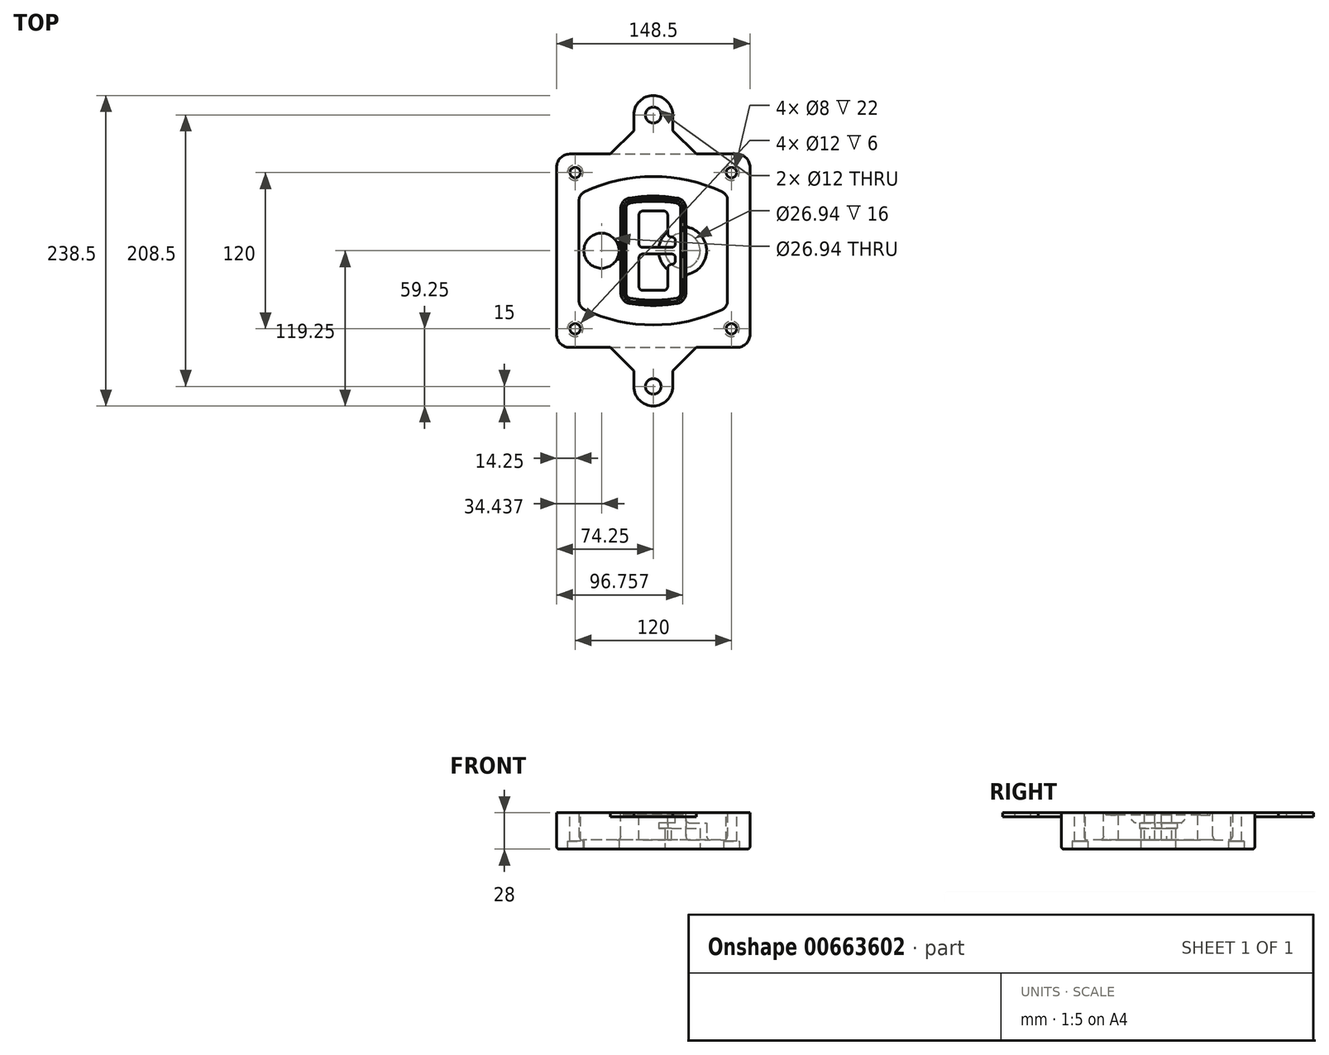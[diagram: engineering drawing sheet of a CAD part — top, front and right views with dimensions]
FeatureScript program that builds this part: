
annotation { "Feature Type Name" : "Feature", "Feature Type Description" : "" }
export const myFeature = defineFeature(function(context is Context, id is Id, definition is map)
    precondition{}
    {
        {
            var Q0;
            Q0=qCreatedBy(makeId("Top.planeOp"),FACE);
            var sketch = newSketch(context, id + "F0", { "sketchPlane" : qUnion([Q0])});
            skPoint(sketch, "E0.rect.middle", {"position": v(0, 0) * mm});
            skLineSegment(sketch, "E1.bottom", {"start": v(-64.25, -74.25) * mm, "end": v(64.25, -74.25) * mm});
            skLineSegment(sketch, "E1.top", {"start": v(-64.25, 74.25) * mm, "end": v(64.25, 74.25) * mm});
            skLineSegment(sketch, "E1.left", {"start": v(-74.25, -64.25) * mm, "end": v(-74.25, 64.25) * mm});
            skLineSegment(sketch, "E1.right", {"start": v(74.25, -64.25) * mm, "end": v(74.25, 64.25) * mm});
            skLineSegment(sketch, "E2", {"start": v(-74.25, 74.25) * mm, "end": v(74.25, -74.25) * mm, "construction": true});
            skLineSegment(sketch, "E3", {"start": v(74.25, 74.25) * mm, "end": v(-74.25, -74.25) * mm, "construction": true});
            skCircle(sketch, "E4", {"center": v(-60, 60) * mm, "radius": 4 * mm});
            skCircle(sketch, "E5", {"center": v(60, 60) * mm, "radius": 4 * mm});
            skCircle(sketch, "E6", {"center": v(60, -60) * mm, "radius": 4 * mm});
            skCircle(sketch, "E7", {"center": v(-60, -60) * mm, "radius": 4 * mm});
            skLineSegment(sketch, "E8", {"start": v(-60, 60) * mm, "end": v(60, 60) * mm, "construction": true});
            skLineSegment(sketch, "E9", {"start": v(60, 60) * mm, "end": v(60, -60) * mm, "construction": true});
            skLineSegment(sketch, "E10", {"start": v(60, -60) * mm, "end": v(-60, -60) * mm, "construction": true});
            skLineSegment(sketch, "E11", {"start": v(-60, -60) * mm, "end": v(-60, 60) * mm, "construction": true});
            skLineSegment(sketch, "E12", {"start": v(-60, 38.83) * mm, "end": v(-60, -38.83) * mm});
            skLineSegment(sketch, "E13", {"start": v(60, 38.83) * mm, "end": v(60, -38.83) * mm});
            skArc(sketch, "E14", {"start": v(54.26, 47.88) * mm, "mid": v(0, 60) * mm, "end": v(-54.26, 47.88) * mm});
            skArc(sketch, "E15", {"start": v(-54.26, -47.88) * mm, "mid": v(0, -60) * mm, "end": v(54.26, -47.88) * mm});
            skLineSegment(sketch, "E16", {"start": v(-60, 0) * mm, "end": v(60, 0) * mm, "construction": true});
            skPoint(sketch, "E17.visualSharp", {"position": v(-60, -45) * mm});
            skArc(sketch, "E17.filletArc", {"start": v(-60, -38.83) * mm, "mid": v(-58.44, -44.2) * mm, "end": v(-54.26, -47.88) * mm});
            skPoint(sketch, "E18.visualSharp", {"position": v(-60, 45) * mm});
            skArc(sketch, "E18.filletArc", {"start": v(-54.26, 47.88) * mm, "mid": v(-58.44, 44.2) * mm, "end": v(-60, 38.83) * mm});
            skPoint(sketch, "E19.visualSharp", {"position": v(60, 45) * mm});
            skArc(sketch, "E19.filletArc", {"start": v(60, 38.83) * mm, "mid": v(58.44, 44.2) * mm, "end": v(54.26, 47.88) * mm});
            skPoint(sketch, "E20.visualSharp", {"position": v(60, -45) * mm});
            skArc(sketch, "E20.filletArc", {"start": v(54.26, -47.88) * mm, "mid": v(58.44, -44.2) * mm, "end": v(60, -38.83) * mm});
            skPoint(sketch, "E21.visualSharp", {"position": v(-74.25, 74.25) * mm});
            skArc(sketch, "E21.filletArc", {"start": v(-64.25, 74.25) * mm, "mid": v(-71.32, 71.32) * mm, "end": v(-74.25, 64.25) * mm});
            skPoint(sketch, "E22.visualSharp", {"position": v(74.25, 74.25) * mm});
            skArc(sketch, "E22.filletArc", {"start": v(74.25, 64.25) * mm, "mid": v(71.32, 71.32) * mm, "end": v(64.25, 74.25) * mm});
            skPoint(sketch, "E23.visualSharp", {"position": v(74.25, -74.25) * mm});
            skArc(sketch, "E23.filletArc", {"start": v(64.25, -74.25) * mm, "mid": v(71.32, -71.32) * mm, "end": v(74.25, -64.25) * mm});
            skPoint(sketch, "E24.visualSharp", {"position": v(-74.25, -74.25) * mm});
            skArc(sketch, "E24.filletArc", {"start": v(-74.25, -64.25) * mm, "mid": v(-71.32, -71.32) * mm, "end": v(-64.25, -74.25) * mm});
            skArc(sketch, "E25.0", {"start": v(57, 38.83) * mm, "mid": v(55.9, 42.58) * mm, "end": v(52.98, 45.17) * mm});
            skLineSegment(sketch, "E25.1", {"start": v(57, 38.83) * mm, "end": v(57, -38.83) * mm});
            skArc(sketch, "E25.2", {"start": v(52.98, -45.17) * mm, "mid": v(55.9, -42.58) * mm, "end": v(57, -38.83) * mm});
            skArc(sketch, "E25.3", {"start": v(-52.98, -45.17) * mm, "mid": v(0, -57) * mm, "end": v(52.98, -45.17) * mm});
            skArc(sketch, "E25.4", {"start": v(-57, -38.83) * mm, "mid": v(-55.9, -42.58) * mm, "end": v(-52.98, -45.17) * mm});
            skArc(sketch, "E25.5", {"start": v(52.98, 45.17) * mm, "mid": v(0, 57) * mm, "end": v(-52.98, 45.17) * mm});
            skLineSegment(sketch, "E25.6", {"start": v(-57, 38.83) * mm, "end": v(-57, -38.83) * mm});
            skArc(sketch, "E25.7", {"start": v(-52.98, 45.17) * mm, "mid": v(-55.9, 42.58) * mm, "end": v(-57, 38.83) * mm});
            skArc(sketch, "E26.0", {"start": v(-55.96, 51.5) * mm, "mid": v(-61.82, 46.33) * mm, "end": v(-64, 38.83) * mm});
            skArc(sketch, "E26.1", {"start": v(55.96, 51.5) * mm, "mid": v(0, 64) * mm, "end": v(-55.96, 51.5) * mm});
            skArc(sketch, "E26.2", {"start": v(64, 38.83) * mm, "mid": v(61.82, 46.33) * mm, "end": v(55.96, 51.5) * mm});
            skLineSegment(sketch, "E26.3", {"start": v(64, 38.83) * mm, "end": v(64, -38.83) * mm});
            skArc(sketch, "E26.4", {"start": v(55.96, -51.5) * mm, "mid": v(61.82, -46.33) * mm, "end": v(64, -38.83) * mm});
            skLineSegment(sketch, "E26.5", {"start": v(-64, 38.83) * mm, "end": v(-64, -38.83) * mm});
            skArc(sketch, "E26.6", {"start": v(-55.96, -51.5) * mm, "mid": v(0, -64) * mm, "end": v(55.96, -51.5) * mm});
            skArc(sketch, "E26.7", {"start": v(-64, -38.83) * mm, "mid": v(-61.82, -46.33) * mm, "end": v(-55.96, -51.5) * mm});
            skSolve(sketch);
        }
        {
            var Q0;
            Q0=makeQuery(id+"F0.imprint","IMPRINT",FACE,{"disambiguationData":[TD([[makeQuery(id+"F0.imprint","IMPRINT",EDGE,{"derivedFrom":sQuery(id+"F0.wireOp",EDGE,"E1.bottom")}),1.0]])]});
            var Q1;
            Q1=makeQuery(id+"F0.imprint","IMPRINT",FACE,{"disambiguationData":[TD([[makeQuery(id+"F0.imprint","IMPRINT",EDGE,{"derivedFrom":sQuery(id+"F0.wireOp",EDGE,"E12")}),1.0]])]});
            var Q2;
            Q2=makeQuery(id+"F0.imprint","IMPRINT",FACE,{"disambiguationData":[TD([[makeQuery(id+"F0.imprint","IMPRINT",EDGE,{"derivedFrom":sQuery(id+"F0.wireOp",EDGE,"E25.0")}),1.0]])]});
            var Q3;
            Q3=makeQuery(id+"F0.imprint","IMPRINT",FACE,{"disambiguationData":[TD([[makeQuery(id+"F0.imprint","IMPRINT",EDGE,{"derivedFrom":sQuery(id+"F0.wireOp",EDGE,"E12")}),-1.0]])]});
            extrude(context, id + "F1", {"entities" : qUnion([Q0, Q1, Q2, Q3]), "oppositeDirection" : true, "depth" : 25 * mm});
        }
        {
            var Q0;
            Q0=makeQuery(id+"F0.imprint","IMPRINT",FACE,{"disambiguationData":[TD([[makeQuery(id+"F0.imprint","IMPRINT",EDGE,{"derivedFrom":sQuery(id+"F0.wireOp",EDGE,"E12")}),1.0]])]});
            extrude(context, id + "F2", {"entities" : qUnion([Q0]), "operationType" : NewBodyOperationType.ADD, "depth" : 3 * mm});
        }
        {
            var Q0;
            Q0=makeQuery(id+"F0.imprint","IMPRINT",FACE,{"disambiguationData":[TD([[makeQuery(id+"F0.imprint","IMPRINT",EDGE,{"derivedFrom":sQuery(id+"F0.wireOp",EDGE,"E25.0")}),1.0]])]});
            extrude(context, id + "F3", {"entities" : qUnion([Q0]), "operationType" : NewBodyOperationType.REMOVE, "oppositeDirection" : true, "depth" : 18 * mm});
        }
        {
            var Q0;
            Q0=makeQuery(id+"F2.opExtrude","CAP_FACE",FACE,{"disambiguationData":[OSD([sQuery(id+"F0.wireOp",EDGE,"E12"),sQuery(id+"F0.wireOp",EDGE,"E13"),sQuery(id+"F0.wireOp",EDGE,"E14"),sQuery(id+"F0.wireOp",EDGE,"E15"),sQuery(id+"F0.wireOp",EDGE,"E17.filletArc"),sQuery(id+"F0.wireOp",EDGE,"E18.filletArc"),sQuery(id+"F0.wireOp",EDGE,"E19.filletArc"),sQuery(id+"F0.wireOp",EDGE,"E20.filletArc"),sQuery(id+"F0.wireOp",EDGE,"E25.0"),sQuery(id+"F0.wireOp",EDGE,"E25.1"),sQuery(id+"F0.wireOp",EDGE,"E25.2"),sQuery(id+"F0.wireOp",EDGE,"E25.3"),sQuery(id+"F0.wireOp",EDGE,"E25.4"),sQuery(id+"F0.wireOp",EDGE,"E25.5"),sQuery(id+"F0.wireOp",EDGE,"E25.6"),sQuery(id+"F0.wireOp",EDGE,"E25.7")])],"isStart":false});
            var sketch = newSketch(context, id + "F4", { "sketchPlane" : qUnion([Q0])});
            skArc(sketch, "E27.0", {"start": v(-18.34, -40.45) * mm, "mid": v(0, -42) * mm, "end": v(18.34, -40.45) * mm});
            skArc(sketch, "E28.0", {"start": v(18.34, 40.45) * mm, "mid": v(0, 42) * mm, "end": v(-18.34, 40.45) * mm});
            skLineSegment(sketch, "E29", {"start": v(-25, 32.57) * mm, "end": v(-25, -32.57) * mm});
            skLineSegment(sketch, "E30", {"start": v(25, 32.57) * mm, "end": v(25, -32.57) * mm});
            skLineSegment(sketch, "E31", {"start": v(-25, 39.1) * mm, "end": v(25, 39.1) * mm, "construction": true});
            skLineSegment(sketch, "E32", {"start": v(-25, -39.1) * mm, "end": v(25, -39.1) * mm, "construction": true});
            skPoint(sketch, "E33.visualSharp", {"position": v(-25, 39.1) * mm});
            skArc(sketch, "E33.filletArc", {"start": v(-18.34, 40.45) * mm, "mid": v(-23.11, 37.73) * mm, "end": v(-25, 32.57) * mm});
            skPoint(sketch, "E34.visualSharp", {"position": v(25, 39.1) * mm});
            skArc(sketch, "E34.filletArc", {"start": v(25, 32.57) * mm, "mid": v(23.11, 37.73) * mm, "end": v(18.34, 40.45) * mm});
            skPoint(sketch, "E35.visualSharp", {"position": v(25, -39.1) * mm});
            skArc(sketch, "E35.filletArc", {"start": v(18.34, -40.45) * mm, "mid": v(23.11, -37.73) * mm, "end": v(25, -32.57) * mm});
            skPoint(sketch, "E36.visualSharp", {"position": v(-25, -39.1) * mm});
            skArc(sketch, "E36.filletArc", {"start": v(-25, -32.57) * mm, "mid": v(-23.11, -37.73) * mm, "end": v(-18.34, -40.45) * mm});
            skArc(sketch, "E37.0", {"start": v(52.98, 45.17) * mm, "mid": v(0, 57) * mm, "end": v(-52.98, 45.17) * mm});
            skArc(sketch, "E37.1", {"start": v(-52.98, 45.17) * mm, "mid": v(-55.9, 42.58) * mm, "end": v(-57, 38.83) * mm});
            skLineSegment(sketch, "E37.2", {"start": v(-57, 38.83) * mm, "end": v(-57, -38.83) * mm});
            skArc(sketch, "E37.3", {"start": v(-57, -38.83) * mm, "mid": v(-55.9, -42.58) * mm, "end": v(-52.98, -45.17) * mm});
            skArc(sketch, "E37.4", {"start": v(-52.98, -45.17) * mm, "mid": v(0, -57) * mm, "end": v(52.98, -45.17) * mm});
            skArc(sketch, "E37.5", {"start": v(52.98, -45.17) * mm, "mid": v(55.9, -42.58) * mm, "end": v(57, -38.83) * mm});
            skLineSegment(sketch, "E37.6", {"start": v(57, 38.83) * mm, "end": v(57, -38.83) * mm});
            skArc(sketch, "E37.7", {"start": v(57, 38.83) * mm, "mid": v(55.9, 42.58) * mm, "end": v(52.98, 45.17) * mm});
            skLineSegment(sketch, "E38.0", {"start": v(23, 32.57) * mm, "end": v(23, -32.57) * mm});
            skArc(sketch, "E38.1", {"start": v(18, -38.48) * mm, "mid": v(21.58, -36.44) * mm, "end": v(23, -32.57) * mm});
            skArc(sketch, "E38.2", {"start": v(-18, -38.48) * mm, "mid": v(0, -40) * mm, "end": v(18, -38.48) * mm});
            skArc(sketch, "E38.3", {"start": v(-23, -32.57) * mm, "mid": v(-21.58, -36.44) * mm, "end": v(-18, -38.48) * mm});
            skLineSegment(sketch, "E38.4", {"start": v(-23, 32.57) * mm, "end": v(-23, -32.57) * mm});
            skArc(sketch, "E38.5", {"start": v(23, 32.57) * mm, "mid": v(21.58, 36.44) * mm, "end": v(18, 38.48) * mm});
            skArc(sketch, "E38.6", {"start": v(-18, 38.48) * mm, "mid": v(-21.58, 36.44) * mm, "end": v(-23, 32.57) * mm});
            skArc(sketch, "E38.7", {"start": v(18, 38.48) * mm, "mid": v(0, 40) * mm, "end": v(-18, 38.48) * mm});
            skArc(sketch, "E39.0", {"start": v(21, 32.57) * mm, "mid": v(20.06, 35.15) * mm, "end": v(17.67, 36.5) * mm});
            skLineSegment(sketch, "E39.1", {"start": v(21, 32.57) * mm, "end": v(21, -32.57) * mm});
            skArc(sketch, "E39.2", {"start": v(17.67, -36.5) * mm, "mid": v(20.06, -35.15) * mm, "end": v(21, -32.57) * mm});
            skArc(sketch, "E39.3", {"start": v(-17.67, -36.5) * mm, "mid": v(0, -38) * mm, "end": v(17.67, -36.5) * mm});
            skArc(sketch, "E39.4", {"start": v(-21, -32.57) * mm, "mid": v(-20.06, -35.15) * mm, "end": v(-17.67, -36.5) * mm});
            skArc(sketch, "E39.5", {"start": v(17.67, 36.5) * mm, "mid": v(0, 38) * mm, "end": v(-17.67, 36.5) * mm});
            skLineSegment(sketch, "E39.6", {"start": v(-21, 32.57) * mm, "end": v(-21, -32.57) * mm});
            skArc(sketch, "E39.7", {"start": v(-17.67, 36.5) * mm, "mid": v(-20.06, 35.15) * mm, "end": v(-21, 32.57) * mm});
            skLineSegment(sketch, "E40", {"start": v(-25, 0) * mm, "end": v(25, 0) * mm, "construction": true});
            skLineSegment(sketch, "E41", {"start": v(-11, 5.5) * mm, "end": v(-11, 27.5) * mm});
            skLineSegment(sketch, "E42", {"start": v(-8, 30.5) * mm, "end": v(8, 30.5) * mm});
            skLineSegment(sketch, "E43", {"start": v(11, 27.5) * mm, "end": v(11, 13.5) * mm});
            skLineSegment(sketch, "E44", {"start": v(14, 10.5) * mm, "end": v(14, 10.5) * mm});
            skLineSegment(sketch, "E45", {"start": v(17, 7.5) * mm, "end": v(17, 5.5) * mm});
            skLineSegment(sketch, "E46", {"start": v(14, 2.5) * mm, "end": v(-8, 2.5) * mm});
            skPoint(sketch, "E47.visualSharp", {"position": v(-11, 30.5) * mm});
            skArc(sketch, "E47.filletArc", {"start": v(-8, 30.5) * mm, "mid": v(-10.12, 29.62) * mm, "end": v(-11, 27.5) * mm});
            skPoint(sketch, "E48.visualSharp", {"position": v(11, 30.5) * mm});
            skArc(sketch, "E48.filletArc", {"start": v(11, 27.5) * mm, "mid": v(10.12, 29.62) * mm, "end": v(8, 30.5) * mm});
            skPoint(sketch, "E49.visualSharp", {"position": v(11, 10.5) * mm});
            skArc(sketch, "E49.filletArc", {"start": v(11, 13.5) * mm, "mid": v(11.88, 11.38) * mm, "end": v(14, 10.5) * mm});
            skPoint(sketch, "E50.visualSharp", {"position": v(17, 10.5) * mm});
            skArc(sketch, "E50.filletArc", {"start": v(17, 7.5) * mm, "mid": v(16.12, 9.62) * mm, "end": v(14, 10.5) * mm});
            skPoint(sketch, "E51.visualSharp", {"position": v(17, 2.5) * mm});
            skArc(sketch, "E51.filletArc", {"start": v(14, 2.5) * mm, "mid": v(16.12, 3.38) * mm, "end": v(17, 5.5) * mm});
            skPoint(sketch, "E52.visualSharp", {"position": v(-11, 2.5) * mm});
            skArc(sketch, "E52.filletArc", {"start": v(-11, 5.5) * mm, "mid": v(-10.12, 3.38) * mm, "end": v(-8, 2.5) * mm});
            skLineSegment(sketch, "E53.0.MirrorCS", {"start": v(14, -2.5) * mm, "end": v(-8, -2.5) * mm});
            skArc(sketch, "E54.0.MirrorCS", {"start": v(-11, -5.5) * mm, "mid": v(-10.12, -3.38) * mm, "end": v(-8, -2.5) * mm});
            skLineSegment(sketch, "E55.0.MirrorCS", {"start": v(-11, -5.5) * mm, "end": v(-11, -27.5) * mm});
            skArc(sketch, "E56.0.MirrorCS", {"start": v(-8, -30.5) * mm, "mid": v(-10.12, -29.62) * mm, "end": v(-11, -27.5) * mm});
            skLineSegment(sketch, "E57.0.MirrorCS", {"start": v(-8, -30.5) * mm, "end": v(8, -30.5) * mm});
            skArc(sketch, "E58.0.MirrorCS", {"start": v(11, -27.5) * mm, "mid": v(10.12, -29.62) * mm, "end": v(8, -30.5) * mm});
            skLineSegment(sketch, "E59.0.MirrorCS", {"start": v(11, -27.5) * mm, "end": v(11, -13.5) * mm});
            skArc(sketch, "E60.0.MirrorCS", {"start": v(11, -13.5) * mm, "mid": v(11.88, -11.38) * mm, "end": v(14, -10.5) * mm});
            skArc(sketch, "E61.0.MirrorCS", {"start": v(17, -7.5) * mm, "mid": v(16.12, -9.62) * mm, "end": v(14, -10.5) * mm});
            skLineSegment(sketch, "E62.0.MirrorCS", {"start": v(17, -7.5) * mm, "end": v(17, -5.5) * mm});
            skArc(sketch, "E63.0.MirrorCS", {"start": v(14, -2.5) * mm, "mid": v(16.12, -3.38) * mm, "end": v(17, -5.5) * mm});
            skSolve(sketch);
        }
        {
            var Q0;
            Q0=makeQuery(id+"F4.imprint","IMPRINT",FACE,{"disambiguationData":[TD([[makeQuery(id+"F4.imprint","IMPRINT",EDGE,{"derivedFrom":sQuery(id+"F4.wireOp",EDGE,"E27.0")}),1.0]])]});
            var Q1;
            Q1=makeQuery(id+"F4.imprint","IMPRINT",FACE,{"disambiguationData":[TD([[makeQuery(id+"F4.imprint","IMPRINT",EDGE,{"derivedFrom":sQuery(id+"F4.wireOp",EDGE,"E38.0")}),-1.0]])]});
            var Q2;
            Q2=makeQuery(id+"F4.imprint","IMPRINT",FACE,{"disambiguationData":[TD([[makeQuery(id+"F4.imprint","IMPRINT",EDGE,{"derivedFrom":sQuery(id+"F4.wireOp",EDGE,"E39.0")}),1.0]])]});
            extrude(context, id + "F5", {"entities" : qUnion([Q0, Q1, Q2]), "operationType" : NewBodyOperationType.ADD, "endBound" : BoundingType.UP_TO_NEXT, "oppositeDirection" : true, "depth" : 25 * mm});
        }
        {
            var Q0;
            Q0=makeQuery(id+"F4.imprint","IMPRINT",FACE,{"disambiguationData":[TD([[makeQuery(id+"F4.imprint","IMPRINT",EDGE,{"derivedFrom":sQuery(id+"F4.wireOp",EDGE,"E38.0")}),-1.0]])]});
            extrude(context, id + "F6", {"entities" : qUnion([Q0]), "operationType" : NewBodyOperationType.REMOVE, "oppositeDirection" : true, "depth" : 2 * mm});
        }
        {
            var Q0;
            Q0=makeQuery(id+"F1.opExtrude","CAP_FACE",FACE,{"disambiguationData":[OSD([sQuery(id+"F0.wireOp",EDGE,"E1.bottom"),sQuery(id+"F0.wireOp",EDGE,"E1.top"),sQuery(id+"F0.wireOp",EDGE,"E1.left"),sQuery(id+"F0.wireOp",EDGE,"E1.right"),sQuery(id+"F0.wireOp",EDGE,"E4"),sQuery(id+"F0.wireOp",EDGE,"E5"),sQuery(id+"F0.wireOp",EDGE,"E6"),sQuery(id+"F0.wireOp",EDGE,"E7"),sQuery(id+"F0.wireOp",EDGE,"E21.filletArc"),sQuery(id+"F0.wireOp",EDGE,"E22.filletArc"),sQuery(id+"F0.wireOp",EDGE,"E23.filletArc"),sQuery(id+"F0.wireOp",EDGE,"E24.filletArc")])],"isStart":false});
            var sketch = newSketch(context, id + "F7", { "sketchPlane" : qUnion([Q0])});
            skCircle(sketch, "E64", {"center": v(22.5, 0) * mm, "radius": 13.47 * mm});
            skCircle(sketch, "E65", {"center": v(-39.81, 0) * mm, "radius": 13.47 * mm});
            skLineSegment(sketch, "E66", {"start": v(74.25, 0) * mm, "end": v(-74.25, 0) * mm});
            skCircle(sketch, "E67", {"center": v(22.5, 0) * mm, "radius": 18.47 * mm});
            skCircle(sketch, "E68", {"center": v(60, -60) * mm, "radius": 6 * mm});
            skCircle(sketch, "E69", {"center": v(-60, -60) * mm, "radius": 6 * mm});
            skCircle(sketch, "E70", {"center": v(-60, 60) * mm, "radius": 6 * mm});
            skCircle(sketch, "E71", {"center": v(60, 60) * mm, "radius": 6 * mm});
            skSolve(sketch);
        }
        {
            var Q0;
            {var subQ1=sQuery(id+"F7.wireOp",EDGE,"E66");var subQ4=sQuery(id+"F7.wireOp",EDGE,"E64");var subQ6=makeQuery(id+"F7.imprint","INTERSECT",VERTEX,{"disambiguationData":[OD(0.0)],"derivedFrom":[subQ4,subQ1]});Q0=makeQuery(id+"F7.imprint","IMPRINT",FACE,{"disambiguationData":[TD([[makeQuery(id+"F7.imprint","IMPRINT",EDGE,{"disambiguationData":[TD([[subQ6,-1.0]])],"derivedFrom":subQ4}),-1.0]])]});}
            var Q1;
            {var subQ0=sQuery(id+"F7.wireOp",EDGE,"E66");var subQ1=sQuery(id+"F7.wireOp",EDGE,"E64");var subQ3=makeQuery(id+"F7.imprint","INTERSECT",VERTEX,{"disambiguationData":[OD(0.0)],"derivedFrom":[subQ1,subQ0]});Q1=makeQuery(id+"F7.imprint","IMPRINT",FACE,{"disambiguationData":[TD([[makeQuery(id+"F7.imprint","IMPRINT",EDGE,{"disambiguationData":[TD([[subQ3,-1.0]])],"derivedFrom":subQ1}),1.0]])]});}
            var Q2;
            {var subQ0=sQuery(id+"F7.wireOp",EDGE,"E66");var subQ1=sQuery(id+"F7.wireOp",EDGE,"E64");var subQ3=makeQuery(id+"F7.imprint","INTERSECT",VERTEX,{"disambiguationData":[OD(0.0)],"derivedFrom":[subQ1,subQ0]});Q2=makeQuery(id+"F7.imprint","IMPRINT",FACE,{"disambiguationData":[TD([[makeQuery(id+"F7.imprint","IMPRINT",EDGE,{"disambiguationData":[TD([[subQ3,1.0]])],"derivedFrom":subQ1}),1.0]])]});}
            var Q3;
            {var subQ1=sQuery(id+"F7.wireOp",EDGE,"E66");var subQ4=sQuery(id+"F7.wireOp",EDGE,"E64");var subQ6=makeQuery(id+"F7.imprint","INTERSECT",VERTEX,{"disambiguationData":[OD(0.0)],"derivedFrom":[subQ4,subQ1]});Q3=makeQuery(id+"F7.imprint","IMPRINT",FACE,{"disambiguationData":[TD([[makeQuery(id+"F7.imprint","IMPRINT",EDGE,{"disambiguationData":[TD([[subQ6,1.0]])],"derivedFrom":subQ4}),-1.0]])]});}
            extrude(context, id + "F8", {"entities" : qUnion([Q0, Q1, Q2, Q3]), "operationType" : NewBodyOperationType.ADD, "oppositeDirection" : true, "depth" : 20 * mm});
        }
        {
            var Q0;
            {var subQ0=sQuery(id+"F7.wireOp",EDGE,"E66");var subQ1=sQuery(id+"F7.wireOp",EDGE,"E64");var subQ3=makeQuery(id+"F7.imprint","INTERSECT",VERTEX,{"disambiguationData":[OD(0.0)],"derivedFrom":[subQ1,subQ0]});Q0=makeQuery(id+"F7.imprint","IMPRINT",FACE,{"disambiguationData":[TD([[makeQuery(id+"F7.imprint","IMPRINT",EDGE,{"disambiguationData":[TD([[subQ3,-1.0]])],"derivedFrom":subQ1}),1.0]])]});}
            var Q1;
            {var subQ0=sQuery(id+"F7.wireOp",EDGE,"E66");var subQ1=sQuery(id+"F7.wireOp",EDGE,"E64");var subQ3=makeQuery(id+"F7.imprint","INTERSECT",VERTEX,{"disambiguationData":[OD(0.0)],"derivedFrom":[subQ1,subQ0]});Q1=makeQuery(id+"F7.imprint","IMPRINT",FACE,{"disambiguationData":[TD([[makeQuery(id+"F7.imprint","IMPRINT",EDGE,{"disambiguationData":[TD([[subQ3,1.0]])],"derivedFrom":subQ1}),1.0]])]});}
            extrude(context, id + "F9", {"entities" : qUnion([Q0, Q1]), "operationType" : NewBodyOperationType.REMOVE, "oppositeDirection" : true, "depth" : 16 * mm});
        }
        {
            var Q0;
            {var subQ0=sQuery(id+"F7.wireOp",EDGE,"E66");var subQ1=sQuery(id+"F7.wireOp",EDGE,"E65");var subQ3=makeQuery(id+"F7.imprint","INTERSECT",VERTEX,{"disambiguationData":[OD(0.0)],"derivedFrom":[subQ1,subQ0]});Q0=makeQuery(id+"F7.imprint","IMPRINT",FACE,{"disambiguationData":[TD([[makeQuery(id+"F7.imprint","IMPRINT",EDGE,{"disambiguationData":[TD([[subQ3,-1.0]])],"derivedFrom":subQ1}),1.0]])]});}
            var Q1;
            {var subQ0=sQuery(id+"F7.wireOp",EDGE,"E66");var subQ1=sQuery(id+"F7.wireOp",EDGE,"E65");var subQ3=makeQuery(id+"F7.imprint","INTERSECT",VERTEX,{"disambiguationData":[OD(0.0)],"derivedFrom":[subQ1,subQ0]});Q1=makeQuery(id+"F7.imprint","IMPRINT",FACE,{"disambiguationData":[TD([[makeQuery(id+"F7.imprint","IMPRINT",EDGE,{"disambiguationData":[TD([[subQ3,1.0]])],"derivedFrom":subQ1}),1.0]])]});}
            extrude(context, id + "F10", {"entities" : qUnion([Q0, Q1]), "operationType" : NewBodyOperationType.REMOVE, "oppositeDirection" : true, "depth" : 25 * mm});
        }
        {
            var Q0;
            Q0=makeQuery(id+"F7.imprint","IMPRINT",FACE,{"disambiguationData":[TD([[makeQuery(id+"F7.imprint","IMPRINT",EDGE,{"derivedFrom":sQuery(id+"F7.wireOp",EDGE,"E68")}),1.0]])]});
            var Q1;
            Q1=makeQuery(id+"F7.imprint","IMPRINT",FACE,{"disambiguationData":[TD([[makeQuery(id+"F7.imprint","IMPRINT",EDGE,{"derivedFrom":makeQuery(id+"F1.opExtrude","CAP_EDGE",EDGE,{"disambiguationData":[OSD([sQuery(id+"F0.wireOp",EDGE,"E5")])],"isStart":false})}),-1.0]])]});
            var Q2;
            Q2=makeQuery(id+"F7.imprint","IMPRINT",FACE,{"disambiguationData":[TD([[makeQuery(id+"F7.imprint","IMPRINT",EDGE,{"derivedFrom":sQuery(id+"F7.wireOp",EDGE,"E69")}),1.0]])]});
            var Q3;
            Q3=makeQuery(id+"F7.imprint","IMPRINT",FACE,{"disambiguationData":[TD([[makeQuery(id+"F7.imprint","IMPRINT",EDGE,{"derivedFrom":makeQuery(id+"F1.opExtrude","CAP_EDGE",EDGE,{"disambiguationData":[OSD([sQuery(id+"F0.wireOp",EDGE,"E4")])],"isStart":false})}),-1.0]])]});
            var Q4;
            Q4=makeQuery(id+"F7.imprint","IMPRINT",FACE,{"disambiguationData":[TD([[makeQuery(id+"F7.imprint","IMPRINT",EDGE,{"derivedFrom":sQuery(id+"F7.wireOp",EDGE,"E70")}),1.0]])]});
            var Q5;
            Q5=makeQuery(id+"F7.imprint","IMPRINT",FACE,{"disambiguationData":[TD([[makeQuery(id+"F7.imprint","IMPRINT",EDGE,{"derivedFrom":makeQuery(id+"F1.opExtrude","CAP_EDGE",EDGE,{"disambiguationData":[OSD([sQuery(id+"F0.wireOp",EDGE,"E7")])],"isStart":false})}),-1.0]])]});
            var Q6;
            Q6=makeQuery(id+"F7.imprint","IMPRINT",FACE,{"disambiguationData":[TD([[makeQuery(id+"F7.imprint","IMPRINT",EDGE,{"derivedFrom":sQuery(id+"F7.wireOp",EDGE,"E71")}),1.0]])]});
            var Q7;
            Q7=makeQuery(id+"F7.imprint","IMPRINT",FACE,{"disambiguationData":[TD([[makeQuery(id+"F7.imprint","IMPRINT",EDGE,{"derivedFrom":makeQuery(id+"F1.opExtrude","CAP_EDGE",EDGE,{"disambiguationData":[OSD([sQuery(id+"F0.wireOp",EDGE,"E6")])],"isStart":false})}),-1.0]])]});
            extrude(context, id + "F11", {"entities" : qUnion([Q0, Q1, Q2, Q3, Q4, Q5, Q6, Q7]), "operationType" : NewBodyOperationType.REMOVE, "oppositeDirection" : true, "depth" : 6 * mm});
        }
        {
            var Q0;
            Q0=makeQuery(id+"F9.boolean.opBoolean","COPY",FACE,{"derivedFrom":makeQuery(id+"F9.opExtrude","CAP_FACE",FACE,{"disambiguationData":[OSD([sQuery(id+"F7.wireOp",EDGE,"E64")])],"isStart":false})});
            var sketch = newSketch(context, id + "F12", { "sketchPlane" : qUnion([Q0])});
            skArc(sketch, "E72.0", {"start": v(11, 14.45) * mm, "mid": v(6.45, 9.13) * mm, "end": v(4.2, 2.5) * mm});
            skArc(sketch, "E72.1", {"start": v(4.2, -2.5) * mm, "mid": v(6.45, -9.13) * mm, "end": v(11, -14.45) * mm});
            skLineSegment(sketch, "E73", {"start": v(4.2, -2.5) * mm, "end": v(14, -2.5) * mm});
            skLineSegment(sketch, "E74.0", {"start": v(14, 2.5) * mm, "end": v(4.2, 2.5) * mm});
            skArc(sketch, "E74.1", {"start": v(14, 2.5) * mm, "mid": v(16.12, 3.38) * mm, "end": v(17, 5.5) * mm});
            skLineSegment(sketch, "E74.2", {"start": v(17, 7.5) * mm, "end": v(17, 5.5) * mm});
            skArc(sketch, "E74.3", {"start": v(17, 7.5) * mm, "mid": v(16.12, 9.62) * mm, "end": v(14, 10.5) * mm});
            skArc(sketch, "E74.4", {"start": v(11, 13.5) * mm, "mid": v(11.88, 11.38) * mm, "end": v(14, 10.5) * mm});
            skLineSegment(sketch, "E74.5", {"start": v(11, 14.45) * mm, "end": v(11, 13.5) * mm});
            skLineSegment(sketch, "E74.7", {"start": v(14, -2.5) * mm, "end": v(4.2, -2.5) * mm});
            skArc(sketch, "E74.8", {"start": v(14, -2.5) * mm, "mid": v(16.12, -3.38) * mm, "end": v(17, -5.5) * mm});
            skLineSegment(sketch, "E74.9", {"start": v(17, -7.5) * mm, "end": v(17, -5.5) * mm});
            skArc(sketch, "E74.10", {"start": v(17, -7.5) * mm, "mid": v(16.12, -9.62) * mm, "end": v(14, -10.5) * mm});
            skArc(sketch, "E74.11", {"start": v(11, -13.5) * mm, "mid": v(11.88, -11.38) * mm, "end": v(14, -10.5) * mm});
            skLineSegment(sketch, "E74.12", {"start": v(11, -14.45) * mm, "end": v(11, -13.5) * mm});
            skPoint(sketch, "E75.orphan", {"position": v(11, -27.5) * mm});
            skPoint(sketch, "E76.orphan", {"position": v(-8, -2.5) * mm});
            skPoint(sketch, "E77.orphan", {"position": v(-8, 2.5) * mm});
            skPoint(sketch, "E78.orphan", {"position": v(11, 27.5) * mm});
            skSolve(sketch);
        }
        {
            var Q0;
            {var subQ7=sQuery(id+"F12.wireOp",EDGE,"E72.0");var subQ14=sQuery(id+"F12.wireOp",EDGE,"E72.1");var subQ16=sQuery(id+"F12.wireOp",EDGE,"E74.1");var subQ18=sQuery(id+"F12.wireOp",EDGE,"E74.8");Q0=qUnion([makeQuery(id+"F12.imprint","IMPRINT",FACE,{"disambiguationData":[TD([[makeQuery(id+"F12.imprint","IMPRINT",EDGE,{"derivedFrom":subQ7}),1.0]])]}),makeQuery(id+"F12.imprint","IMPRINT",FACE,{"disambiguationData":[TD([[makeQuery(id+"F12.imprint","IMPRINT",EDGE,{"derivedFrom":subQ14}),1.0]])]}),makeQuery(id+"F12.imprint","IMPRINT",FACE,{"disambiguationData":[TD([[makeQuery(id+"F12.imprint","IMPRINT",EDGE,{"derivedFrom":subQ16}),1.0]])]}),makeQuery(id+"F12.imprint","IMPRINT",FACE,{"disambiguationData":[TD([[makeQuery(id+"F12.imprint","IMPRINT",EDGE,{"derivedFrom":subQ18}),-1.0]])]})]);}
            var Q1;
            Q1=makeQuery(id+"F5.boolean.opBoolean","SPLIT",FACE,{"disambiguationData":[TD([makeQuery(id+"F5.opExtrude","SWEPT_FACE",FACE,{"disambiguationData":[OSD([sQuery(id+"F4.wireOp",EDGE,"E41")])]})])],"derivedFrom":makeQuery(id+"F3.boolean.opBoolean","COPY",FACE,{"derivedFrom":makeQuery(id+"F3.opExtrude","CAP_FACE",FACE,{"disambiguationData":[OSD([sQuery(id+"F0.wireOp",EDGE,"E25.0"),sQuery(id+"F0.wireOp",EDGE,"E25.1"),sQuery(id+"F0.wireOp",EDGE,"E25.2"),sQuery(id+"F0.wireOp",EDGE,"E25.3"),sQuery(id+"F0.wireOp",EDGE,"E25.4"),sQuery(id+"F0.wireOp",EDGE,"E25.5"),sQuery(id+"F0.wireOp",EDGE,"E25.6"),sQuery(id+"F0.wireOp",EDGE,"E25.7")])],"isStart":false})})});
            extrude(context, id + "F13", {"entities" : qUnion([Q0]), "operationType" : NewBodyOperationType.REMOVE, "endBound" : BoundingType.UP_TO_SURFACE, "endBoundEntityFace" : qUnion([Q1]), "depth" : 25 * mm});
        }
        {
            var Q0;
            Q0=makeQuery(id+"F3.boolean.opBoolean","COPY",EDGE,{"derivedFrom":makeQuery(id+"F3.opExtrude","CAP_EDGE",EDGE,{"disambiguationData":[OSD([sQuery(id+"F0.wireOp",EDGE,"E25.6")])],"isStart":false})});
            var Q1;
            Q1=makeQuery(id+"F8.boolean.opBoolean","INTERSECT",EDGE,{"derivedFrom":[makeQuery(id+"F5.opExtrude","SWEPT_FACE",FACE,{"disambiguationData":[OSD([sQuery(id+"F4.wireOp",EDGE,"E30")])]}),makeQuery(id+"F8.opExtrude","CAP_FACE",FACE,{"disambiguationData":[OSD([sQuery(id+"F7.wireOp",EDGE,"E67")])],"isStart":false})]});
            var Q2;
            Q2=makeQuery(id+"F8.boolean.opBoolean","INTERSECT",EDGE,{"disambiguationData":[OD(1.0)],"derivedFrom":[makeQuery(id+"F5.opExtrude","SWEPT_FACE",FACE,{"disambiguationData":[OSD([sQuery(id+"F4.wireOp",EDGE,"E30")])]}),makeQuery(id+"F8.opExtrude","SWEPT_FACE",FACE,{"disambiguationData":[OSD([sQuery(id+"F7.wireOp",EDGE,"E67")])]})]});
            var Q3;
            {var subQ0=sQuery(id+"F4.wireOp",EDGE,"E30");Q3=makeQuery(id+"F8.boolean.opBoolean","SPLIT",EDGE,{"disambiguationData":[TD([makeQuery(id+"F5.opExtrude","SWEPT_FACE",FACE,{"disambiguationData":[OSD([sQuery(id+"F4.wireOp",EDGE,"E35.filletArc")])]})])],"derivedFrom":makeQuery(id+"F5.opExtrude","CAP_EDGE",EDGE,{"disambiguationData":[OSD([subQ0])],"isStart":false})});}
            var Q4;
            {var subQ0=sQuery(id+"F0.wireOp",EDGE,"E25.7");var subQ1=sQuery(id+"F0.wireOp",EDGE,"E25.1");var subQ2=sQuery(id+"F0.wireOp",EDGE,"E25.6");var subQ3=sQuery(id+"F0.wireOp",EDGE,"E25.5");var subQ4=sQuery(id+"F0.wireOp",EDGE,"E25.4");var subQ5=sQuery(id+"F0.wireOp",EDGE,"E25.0");var subQ6=sQuery(id+"F0.wireOp",EDGE,"E25.2");var subQ7=sQuery(id+"F0.wireOp",EDGE,"E25.3");Q4=makeQuery(id+"F8.boolean.opBoolean","INTERSECT",EDGE,{"derivedFrom":[makeQuery(id+"F5.boolean.opBoolean","SPLIT",FACE,{"disambiguationData":[TD([makeQuery(id+"F2.opExtrude","SWEPT_FACE",FACE,{"disambiguationData":[OSD([subQ5])]})])],"derivedFrom":makeQuery(id+"F3.boolean.opBoolean","COPY",FACE,{"derivedFrom":makeQuery(id+"F3.opExtrude","CAP_FACE",FACE,{"disambiguationData":[OSD([subQ5,subQ1,subQ6,subQ7,subQ4,subQ3,subQ2,subQ0])],"isStart":false})})}),makeQuery(id+"F8.opExtrude","SWEPT_FACE",FACE,{"disambiguationData":[OSD([sQuery(id+"F7.wireOp",EDGE,"E67")])]})]});}
            var Q5;
            Q5=makeQuery(id+"F8.boolean.opBoolean","INTERSECT",EDGE,{"disambiguationData":[OD(0.0)],"derivedFrom":[makeQuery(id+"F5.opExtrude","SWEPT_FACE",FACE,{"disambiguationData":[OSD([sQuery(id+"F4.wireOp",EDGE,"E30")])]}),makeQuery(id+"F8.opExtrude","SWEPT_FACE",FACE,{"disambiguationData":[OSD([sQuery(id+"F7.wireOp",EDGE,"E67")])]})]});
            fillet(context, id + "F14", {"entities" : qUnion([Q0, Q1, Q2, Q3, Q4, Q5]), "radius" : 3 * mm, "tangentPropagation" : true, "allowEdgeOverflow" : false});
        }
        {
            var Q0;
            Q0=makeQuery(id+"F1.opExtrude","CAP_EDGE",EDGE,{"disambiguationData":[OSD([sQuery(id+"F0.wireOp",EDGE,"E1.bottom")])],"isStart":false});
            fillet(context, id + "F15", {"entities" : qUnion([Q0]), "radius" : 2 * mm, "tangentPropagation" : true, "allowEdgeOverflow" : false});
        }
        {
            var Q0;
            Q0=qCreatedBy(makeId("Top.planeOp"),FACE);
            var sketch = newSketch(context, id + "F16", { "sketchPlane" : qUnion([Q0])});
            skLineSegment(sketch, "E79", {"start": v(-33, 74.25) * mm, "end": v(-15, 92.25) * mm});
            skLineSegment(sketch, "E80", {"start": v(33, 74.25) * mm, "end": v(15, 92.25) * mm});
            skLineSegment(sketch, "E81", {"start": v(15, 92.25) * mm, "end": v(15, 104.25) * mm});
            skLineSegment(sketch, "E82", {"start": v(-15, 92.25) * mm, "end": v(-15, 104.25) * mm});
            skArc(sketch, "E83", {"start": v(15, 104.25) * mm, "mid": v(0, 119.25) * mm, "end": v(-15, 104.25) * mm});
            skLineSegment(sketch, "E84", {"start": v(0, 104.25) * mm, "end": v(0, 74.25) * mm, "construction": true});
            skCircle(sketch, "E85", {"center": v(0, 104.25) * mm, "radius": 6 * mm});
            skLineSegment(sketch, "E86", {"start": v(0, 74.25) * mm, "end": v(-33, 74.25) * mm});
            skLineSegment(sketch, "E87", {"start": v(0, 74.25) * mm, "end": v(33, 74.25) * mm});
            skLineSegment(sketch, "E88", {"start": v(-74.75, 0) * mm, "end": v(0, 0) * mm, "construction": true});
            skLineSegment(sketch, "E89", {"start": v(0, 0) * mm, "end": v(75.17, 0) * mm, "construction": true});
            skLineSegment(sketch, "E90.MirrorCS", {"start": v(-15, -92.25) * mm, "end": v(-15, -104.25) * mm});
            skLineSegment(sketch, "E91.MirrorCS", {"start": v(15, -92.25) * mm, "end": v(15, -104.25) * mm});
            skLineSegment(sketch, "E92.MirrorCS", {"start": v(33, -74.25) * mm, "end": v(15, -92.25) * mm});
            skLineSegment(sketch, "E93.MirrorCS", {"start": v(0, -74.25) * mm, "end": v(-33, -74.25) * mm});
            skLineSegment(sketch, "E94.MirrorCS", {"start": v(0, -104.25) * mm, "end": v(0, -74.25) * mm, "construction": true});
            skArc(sketch, "E95.MirrorCS", {"start": v(15, -104.25) * mm, "mid": v(0, -119.25) * mm, "end": v(-15, -104.25) * mm});
            skLineSegment(sketch, "E96.MirrorCS", {"start": v(-33, -74.25) * mm, "end": v(-15, -92.25) * mm});
            skLineSegment(sketch, "E97.MirrorCS", {"start": v(0, -74.25) * mm, "end": v(33, -74.25) * mm});
            skCircle(sketch, "E98.MirrorC", {"center": v(0, -104.25) * mm, "radius": 6 * mm});
            skSolve(sketch);
        }
        {
            var Q0;
            Q0=makeQuery(id+"F16.imprint","IMPRINT",FACE,{"disambiguationData":[TD([[makeQuery(id+"F16.imprint","IMPRINT",EDGE,{"derivedFrom":sQuery(id+"F16.wireOp",EDGE,"E79")}),-1.0]])]});
            var Q1;
            {var subQ0=sQuery(id+"F0.wireOp",EDGE,"E21.filletArc");var subQ1=sQuery(id+"F0.wireOp",EDGE,"E7");var subQ2=sQuery(id+"F0.wireOp",EDGE,"E6");var subQ3=sQuery(id+"F0.wireOp",EDGE,"E5");var subQ4=sQuery(id+"F0.wireOp",EDGE,"E4");var subQ5=sQuery(id+"F0.wireOp",EDGE,"E22.filletArc");var subQ6=sQuery(id+"F0.wireOp",EDGE,"E1.bottom");var subQ7=sQuery(id+"F0.wireOp",EDGE,"E1.right");var subQ8=sQuery(id+"F0.wireOp",EDGE,"E1.top");var subQ9=sQuery(id+"F0.wireOp",EDGE,"E1.left");var subQ10=sQuery(id+"F0.wireOp",EDGE,"E23.filletArc");var subQ11=sQuery(id+"F0.wireOp",EDGE,"E24.filletArc");Q1=makeQuery(id+"F2.boolean.opBoolean","SPLIT",FACE,{"disambiguationData":[TD([makeQuery(id+"F1.opExtrude","SWEPT_FACE",FACE,{"disambiguationData":[OSD([subQ6])]})])],"derivedFrom":makeQuery(id+"F1.opExtrude","CAP_FACE",FACE,{"disambiguationData":[OSD([subQ6,subQ8,subQ9,subQ7,subQ4,subQ3,subQ2,subQ1,subQ0,subQ5,subQ10,subQ11])],"isStart":true})});}
            var Q2;
            Q2=makeQuery(id+"F16.imprint","IMPRINT",FACE,{"disambiguationData":[TD([[makeQuery(id+"F16.imprint","IMPRINT",EDGE,{"derivedFrom":sQuery(id+"F16.wireOp",EDGE,"E90.MirrorCS")}),1.0]])]});
            var Q3;
            Q3=makeQuery(id+"F2.opExtrude","CAP_FACE",FACE,{"disambiguationData":[OSD([sQuery(id+"F0.wireOp",EDGE,"E12"),sQuery(id+"F0.wireOp",EDGE,"E13"),sQuery(id+"F0.wireOp",EDGE,"E14"),sQuery(id+"F0.wireOp",EDGE,"E15"),sQuery(id+"F0.wireOp",EDGE,"E17.filletArc"),sQuery(id+"F0.wireOp",EDGE,"E18.filletArc"),sQuery(id+"F0.wireOp",EDGE,"E19.filletArc"),sQuery(id+"F0.wireOp",EDGE,"E20.filletArc"),sQuery(id+"F0.wireOp",EDGE,"E25.0"),sQuery(id+"F0.wireOp",EDGE,"E25.1"),sQuery(id+"F0.wireOp",EDGE,"E25.2"),sQuery(id+"F0.wireOp",EDGE,"E25.3"),sQuery(id+"F0.wireOp",EDGE,"E25.4"),sQuery(id+"F0.wireOp",EDGE,"E25.5"),sQuery(id+"F0.wireOp",EDGE,"E25.6"),sQuery(id+"F0.wireOp",EDGE,"E25.7")])],"isStart":false});
            extrude(context, id + "F17", {"entities" : qUnion([Q0, Q1, Q2]), "operationType" : NewBodyOperationType.ADD, "endBound" : BoundingType.UP_TO_SURFACE, "depth" : 25 * mm, "endBoundEntityFace" : qUnion([Q3]), "offsetDistance" : 25 * mm});
        }
    });
